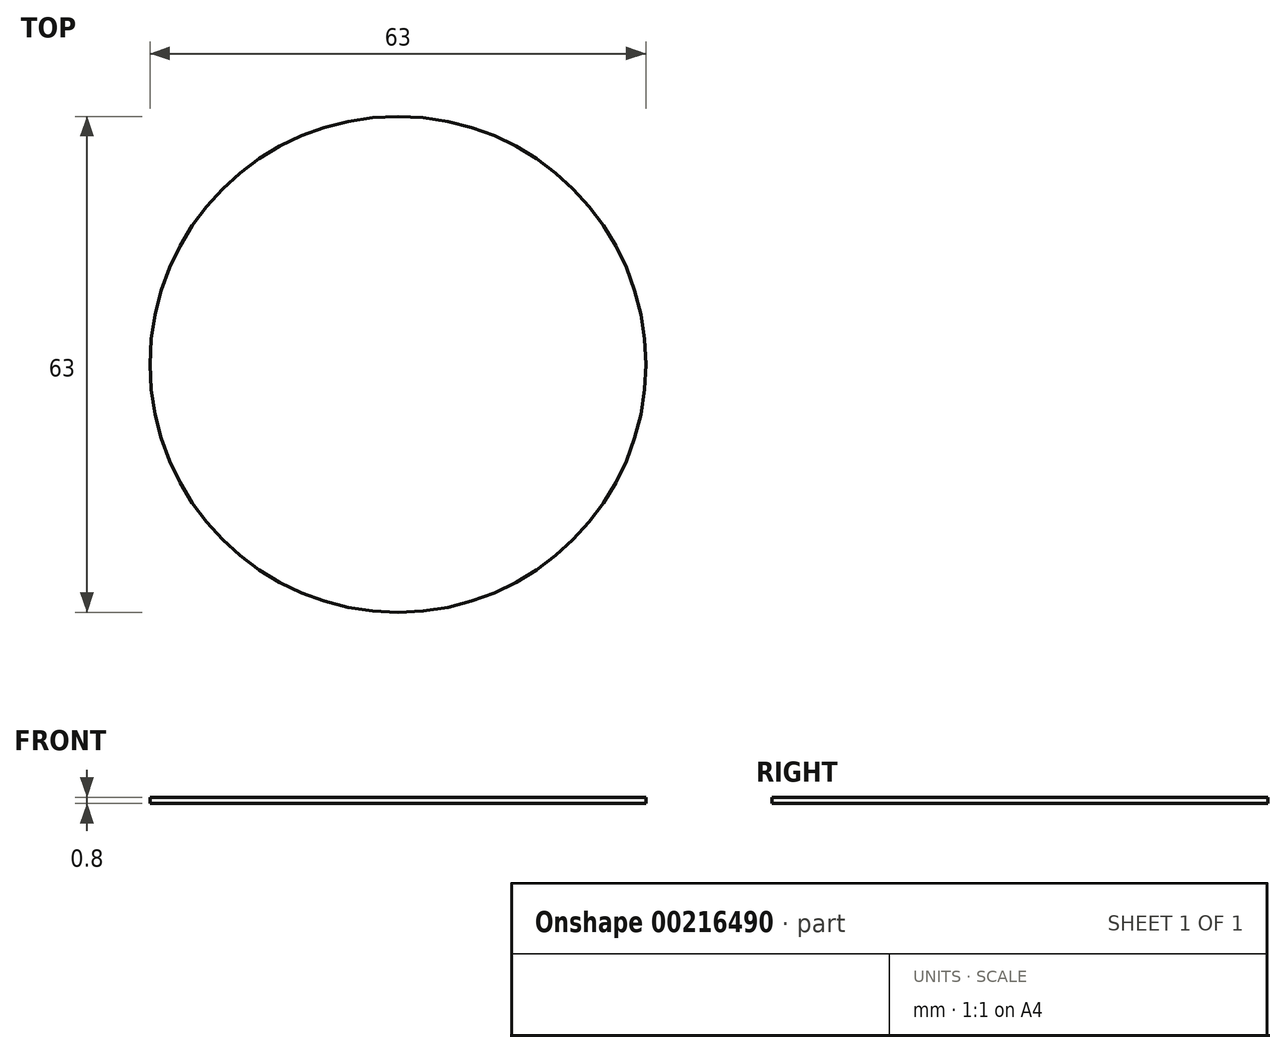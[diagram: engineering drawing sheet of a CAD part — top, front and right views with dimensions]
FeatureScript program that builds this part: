
annotation { "Feature Type Name" : "Feature", "Feature Type Description" : "" }
export const myFeature = defineFeature(function(context is Context, id is Id, definition is map)
    precondition{}
    {
        {
            assignVariable(context, id + "F0", {"variableType" : VariableType.LENGTH, "name" : "Thickness", "lengthValue" : 0.8 * mm});
        }
        {
            var Q0;
            Q0=qCreatedBy(makeId("Top.planeOp"),FACE);
            var sketch = newSketch(context, id + "F1", { "sketchPlane" : qUnion([Q0])});
            skCircle(sketch, "E0", {"center": v(0, 0) * mm, "radius": 31.5 * mm});
            skSolve(sketch);
        }
        {
            var Q0;
            Q0=makeQuery(id+"F1.imprint","IMPRINT",FACE,{"disambiguationData":[TD([[makeQuery(id+"F1.imprint","IMPRINT",EDGE,{"derivedFrom":sQuery(id+"F1.wireOp",EDGE,"E0")}),1.0]])]});
            extrude(context, id + "F2", {"entities" : qUnion([Q0]), "depth" : getVariable(context, 'Thickness'), "offsetDistance" : 25 * mm});
        }
    });
